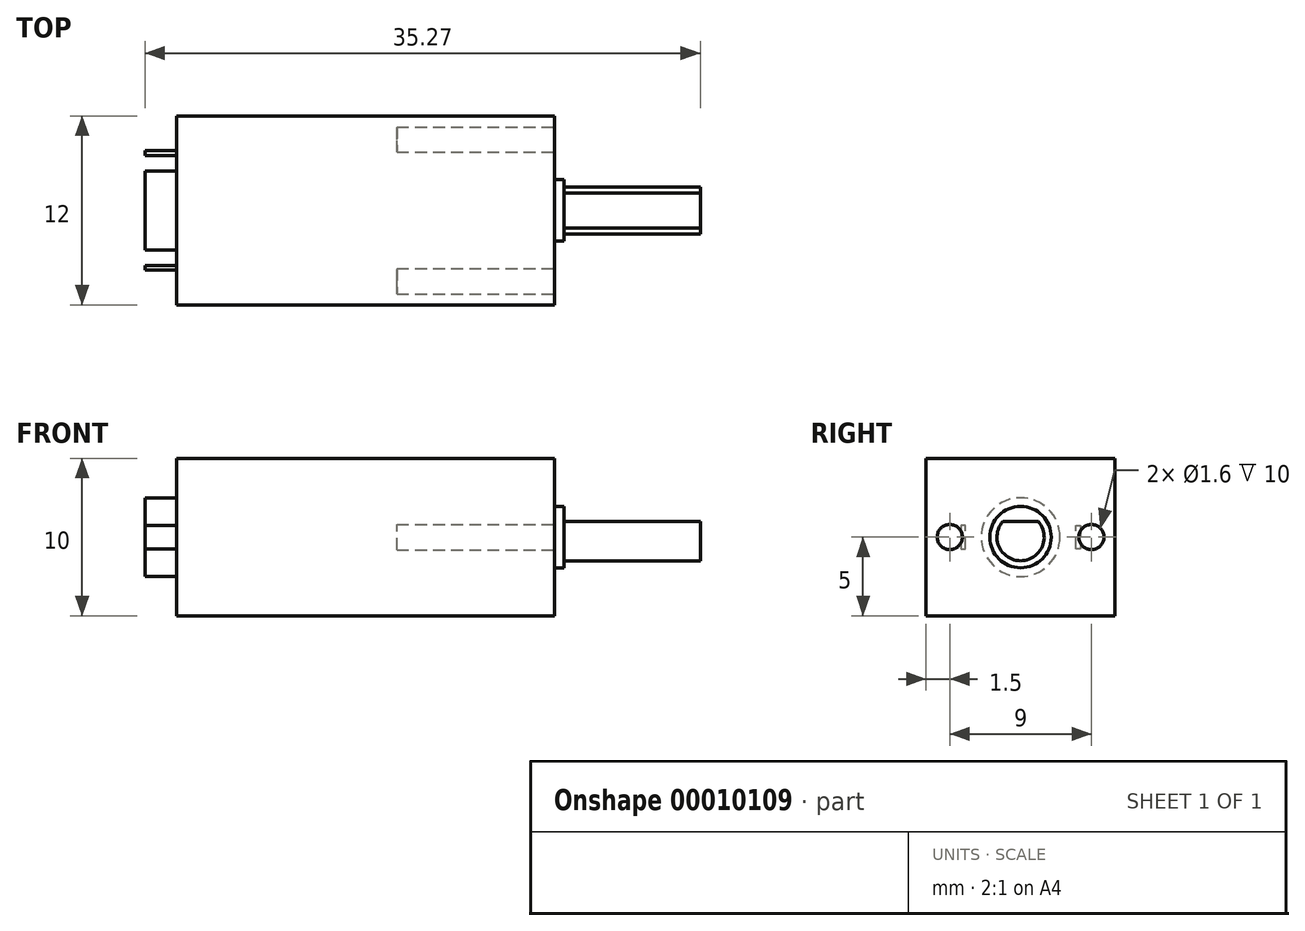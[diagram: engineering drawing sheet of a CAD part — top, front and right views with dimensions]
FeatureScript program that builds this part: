
annotation { "Feature Type Name" : "Feature", "Feature Type Description" : "" }
export const myFeature = defineFeature(function(context is Context, id is Id, definition is map)
    precondition{}
    {
        {
            var Q0;
            Q0=qCreatedBy(makeId("Top.planeOp"),FACE);
            var sketch = newSketch(context, id + "F0", { "sketchPlane" : qUnion([Q0])});
            skLineSegment(sketch, "E0.bottom", {"start": v(0, 0) * mm, "end": v(24, 0) * mm});
            skLineSegment(sketch, "E0.top", {"start": v(0, 12) * mm, "end": v(24, 12) * mm});
            skLineSegment(sketch, "E0.left", {"start": v(0, 0) * mm, "end": v(0, 12) * mm});
            skLineSegment(sketch, "E0.right", {"start": v(24, 0) * mm, "end": v(24, 12) * mm});
            skSolve(sketch);
        }
        {
            var Q0;
            Q0 = qSketchRegion(id + "F0", true);
            extrude(context, id + "F1", {"entities" : qUnion([Q0]), "depth" : 10 * mm});
        }
        {
            var Q0;
            Q0=makeQuery(id+"F1.opExtrude","SWEPT_FACE",FACE,{"disambiguationData":[OSD([sQuery(id+"F0.wireOp",EDGE,"E0.right")])]});
            var sketch = newSketch(context, id + "F2", { "sketchPlane" : qUnion([Q0])});
            skLineSegment(sketch, "E1", {"start": v(0, 0) * mm, "end": v(12, 10) * mm, "construction": true});
            skCircle(sketch, "E2", {"center": v(6, 5) * mm, "radius": 1.95 * mm});
            skSolve(sketch);
        }
        {
            var Q0;
            Q0 = qSketchRegion(id + "F2", true);
            extrude(context, id + "F3", {"entities" : qUnion([Q0]), "operationType" : NewBodyOperationType.ADD, "depth" : 0.6 * mm});
        }
        {
            var Q0;
            Q0=makeQuery(id+"F1.opExtrude","SWEPT_FACE",FACE,{"disambiguationData":[OSD([sQuery(id+"F0.wireOp",EDGE,"E0.right")])]});
            var sketch = newSketch(context, id + "F4", { "sketchPlane" : qUnion([Q0])});
            skArc(sketch, "E3", {"start": v(4.88, 6) * mm, "mid": v(6, 3.5) * mm, "end": v(7.12, 6) * mm});
            skLineSegment(sketch, "E4", {"start": v(4.88, 6) * mm, "end": v(7.12, 6) * mm});
            skSolve(sketch);
        }
        {
            var Q0;
            Q0 = qSketchRegion(id + "F4", true);
            extrude(context, id + "F5", {"entities" : qUnion([Q0]), "operationType" : NewBodyOperationType.ADD, "depth" : 9.27 * mm});
        }
        {
            var Q0;
            Q0=makeQuery(id+"F1.opExtrude","SWEPT_FACE",FACE,{"disambiguationData":[OSD([sQuery(id+"F0.wireOp",EDGE,"E0.right")])]});
            var sketch = newSketch(context, id + "F6", { "sketchPlane" : qUnion([Q0])});
            skCircle(sketch, "E5", {"center": v(1.5, 5) * mm, "radius": 0.8 * mm});
            skCircle(sketch, "E6", {"center": v(10.5, 5) * mm, "radius": 0.8 * mm});
            skLineSegment(sketch, "E7", {"start": v(0, 5) * mm, "end": v(1.5, 5) * mm, "construction": true});
            skLineSegment(sketch, "E8", {"start": v(1.5, 5) * mm, "end": v(6, 5) * mm, "construction": true});
            skLineSegment(sketch, "E9", {"start": v(6, 5) * mm, "end": v(10.5, 5) * mm, "construction": true});
            skLineSegment(sketch, "E10", {"start": v(12, 5) * mm, "end": v(10.5, 5) * mm, "construction": true});
            skSolve(sketch);
        }
        {
            var Q0;
            Q0 = qSketchRegion(id + "F6", true);
            extrude(context, id + "F7", {"entities" : qUnion([Q0]), "operationType" : NewBodyOperationType.REMOVE, "oppositeDirection" : true, "depth" : 10 * mm});
        }
        {
            var Q0;
            Q0=makeQuery(id+"F1.opExtrude","SWEPT_FACE",FACE,{"disambiguationData":[OSD([sQuery(id+"F0.wireOp",EDGE,"E0.left")])]});
            var sketch = newSketch(context, id + "F8", { "sketchPlane" : qUnion([Q0])});
            skLineSegment(sketch, "E11", {"start": v(-12, 5) * mm, "end": v(-9.5, 5) * mm, "construction": true});
            skLineSegment(sketch, "E12", {"start": v(-9.5, 5) * mm, "end": v(-6, 5) * mm, "construction": true});
            skLineSegment(sketch, "E13", {"start": v(-6, 5) * mm, "end": v(-2.5, 5) * mm, "construction": true});
            skLineSegment(sketch, "E14", {"start": v(-2.5, 5) * mm, "end": v(0, 5) * mm, "construction": true});
            skCircle(sketch, "E15", {"center": v(-6, 5) * mm, "radius": 2.5 * mm});
            skLineSegment(sketch, "E16", {"start": v(-9.5, 5) * mm, "end": v(-9.5, 5.75) * mm});
            skLineSegment(sketch, "E17", {"start": v(-9.5, 5.75) * mm, "end": v(-9.8, 5.75) * mm});
            skLineSegment(sketch, "E18", {"start": v(-9.8, 5.75) * mm, "end": v(-9.8, 4.25) * mm});
            skLineSegment(sketch, "E19", {"start": v(-9.8, 4.25) * mm, "end": v(-9.5, 4.25) * mm});
            skLineSegment(sketch, "E20", {"start": v(-9.5, 4.25) * mm, "end": v(-9.5, 5) * mm});
            skLineSegment(sketch, "E21", {"start": v(-6, 10) * mm, "end": v(-6, 0) * mm, "construction": true});
            skLineSegment(sketch, "E22.0.MirrorCS", {"start": v(-2.2, 4.25) * mm, "end": v(-2.5, 4.25) * mm});
            skLineSegment(sketch, "E22.1.MirrorCS", {"start": v(-2.5, 4.25) * mm, "end": v(-2.5, 5) * mm});
            skLineSegment(sketch, "E22.2.MirrorCS", {"start": v(-2.5, 5) * mm, "end": v(-2.5, 5.75) * mm});
            skLineSegment(sketch, "E22.3.MirrorCS", {"start": v(-2.2, 5.75) * mm, "end": v(-2.2, 4.25) * mm});
            skLineSegment(sketch, "E22.4.MirrorCS", {"start": v(-2.5, 5.75) * mm, "end": v(-2.2, 5.75) * mm});
            skSolve(sketch);
        }
        {
            var Q0;
            Q0 = qSketchRegion(id + "F8", true);
            extrude(context, id + "F9", {"entities" : qUnion([Q0]), "operationType" : NewBodyOperationType.ADD, "depth" : 2 * mm});
        }
    });
